# Revit family: LTV73
name_source: partatom
category: Lighting Fixtures
units: mm (PartAtom-declared; Revit-internal decimal feet)

## family parameters
Cut with Voids When Loaded = No
Host = Face
Light Source = Yes
Part Type = Normal
Room Calculation Point = No
Round Connector Dimension = Use Diameter
Shared = No

## types (1)
- LTV73
    Apparent Load = 0 VA
    Assembly Code = D5020200
    Color Filter = 16777215
    Composite Housing material = Plastic-Fiberglass
    Default Elevation = 0"
    Description = Concealed In-grade Luminare
    Dimming Lamp Color Temperature Shift = <None>
    Dome Height = 1 1/2"
    Finish = Cast Bronze, Natural Finish
    Frequency = 60 Hz
    Full Load Current = 0 A
    Glass Material = Glass-Clear
    Initial Lumens = 0.00 lm
    Kim Lighting IES File = ltv73-18led.ies
    Lamp = LED
    Lens Ring Material = Metal-Bronze
    Manufacturer = KIM Lighting
    MasterFormat Number = 26 56 29
    MasterFormat Title = Site Lighting
    Model = LTV73
    Note Text = LF
    Note Visible = Yes
    Number of Poles = 1
    OmniClass Number = 23-80 70 14 11 21
    OmniClass Title = Buried Uplights
    Power Factor = 1
    Series = In-grade
    Tilt Angle = 90.00°
    Type Comments = Lighting Fixture
    URL = https://www.currentlighting.com
    Voltage = 120 V
    Wattage Comments = 18 Watt LED

## geometry (parser evidence)
native form markers: Sweep x3
no freeform markers — native parametric forms only
